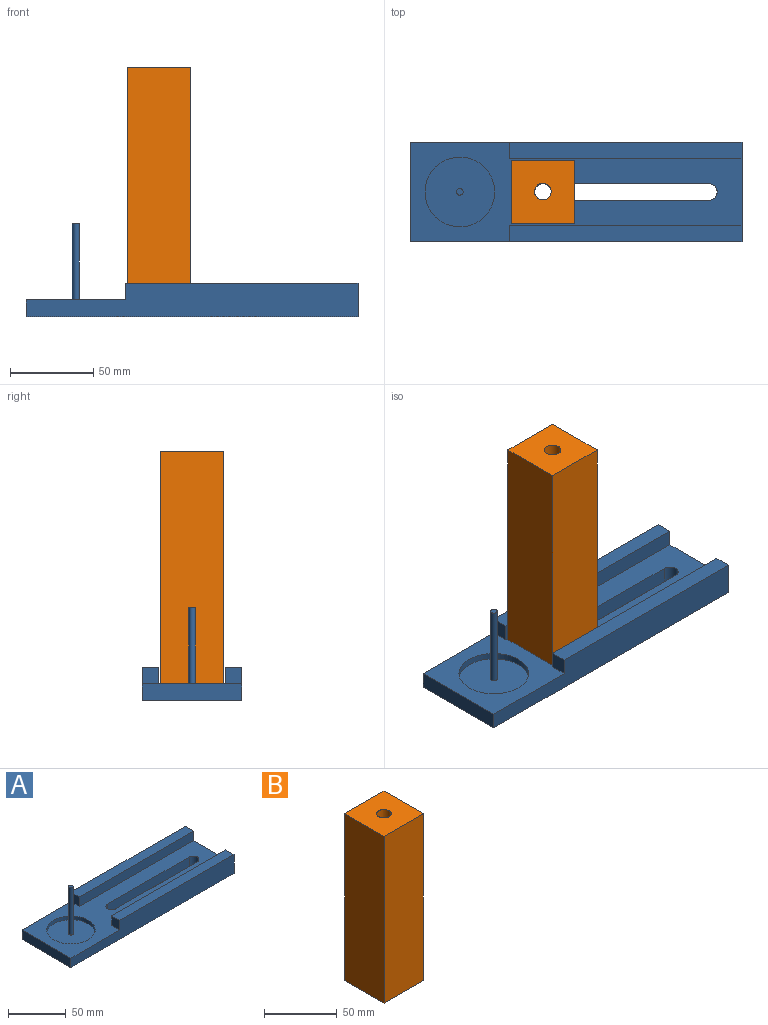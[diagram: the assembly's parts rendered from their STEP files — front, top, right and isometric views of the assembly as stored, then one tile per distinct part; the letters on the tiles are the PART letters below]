
ASSEMBLY  parts=2 mates=2
PART A: 20 faces, bbox 200x60x56 mm
  f0: plane 200x20mm, normal (0,-1,0), area 3400mm2, adj f1,f8,f9,f10,f14,f16
  f1: plane 60x20mm, normal (1,0,0), area 800mm2, adj f0,f2,f9,f10,f12,f13,f15,f16
  f2: plane 200x20mm, normal (0,1,0), area 3400mm2, adj f1,f8,f9,f10,f11,f13
  f3: plane 100x10mm, normal (0,1,0), area 1000mm2, adj f4,f7,f9,f10
  f4: cylinder r=5mm len=10mm, axis (0,0,-1), area 157.1mm2, adj f3,f5,f9,f10
  f5: plane 100x10mm, normal (0,-1,0), area 1000mm2, adj f4,f7,f9,f10
  f6: cylinder r=21mm len=42mm, axis (0,0,-1), area 527.8mm2, adj f9,f17
  f7: cylinder r=5mm len=10mm, axis (0,0,-1), area 157.1mm2, adj f3,f5,f9,f10
  f8: plane 60x10mm, normal (-1,0,0), area 600mm2, adj f0,f2,f9,f10
  f9: plane 200x60mm, normal (0,0,1), area 6736mm2, adj f0,f1,f2,f3,f4,f5,f6,f7
  f10: plane 200x60mm, normal (0,0,-1), area 10921.5mm2, adj f0,f1,f2,f3,f4,f5,f7,f8
  f11: plane 10x10mm, normal (-1,0,0), area 100mm2, adj f2,f9,f12,f13
  f12: plane 140x10mm, normal (0,-1,0), area 1400mm2, adj f1,f9,f11,f13
  f13: plane 140x10mm, normal (0,0,1), area 1400mm2, adj f1,f2,f11,f12
  f14: plane 10x10mm, normal (-1,0,0), area 100mm2, adj f0,f9,f15,f16
  f15: plane 140x10mm, normal (0,1,0), area 1400mm2, adj f1,f9,f14,f16
  f16: plane 140x10mm, normal (0,0,1), area 1400mm2, adj f0,f1,f14,f15
  f17: plane 42x42mm, normal (0,0,1), area 1372.9mm2, adj f6,f18
  f18: cylinder r=2mm len=50mm, axis (0,0,-1), area 628.3mm2, adj f17,f19
  f19: plane 4x4mm, normal (0,0,1), area 12.6mm2, adj f18
PART B: 7 faces, bbox 38x38x140 mm
  f0: plane 140x38mm, normal (-1,0,0), area 5320mm2, adj f1,f4,f5,f6
  f1: plane 140x38mm, normal (0,-1,0), area 5320mm2, adj f0,f2,f5,f6
  f2: plane 140x38mm, normal (1,0,0), area 5320mm2, adj f1,f4,f5,f6
  f3: cylinder r=5mm len=140mm, axis (0,0,-1), area 4398.2mm2, adj f5,f6
  f4: plane 140x38mm, normal (0,1,0), area 5320mm2, adj f0,f2,f5,f6
  f5: plane 38x38mm, normal (0,0,1), area 1365.5mm2, adj f0,f1,f2,f3,f4
  f6: plane 38x38mm, normal (0,0,-1), area 1365.5mm2, adj f0,f1,f2,f3,f4
PLACE A t=(83.43,181.75,139.96)mm
PLACE B t=(21.44,162.75,149.96)mm
MATE parallel A.f9 <-> B.f3  axis (0,0,1) through (140.43,186.75,149.96)mm
MATE pin_slot A.f4 <-> B.f3  axis (0,0,1) through (40.43,181.75,149.96)mm
